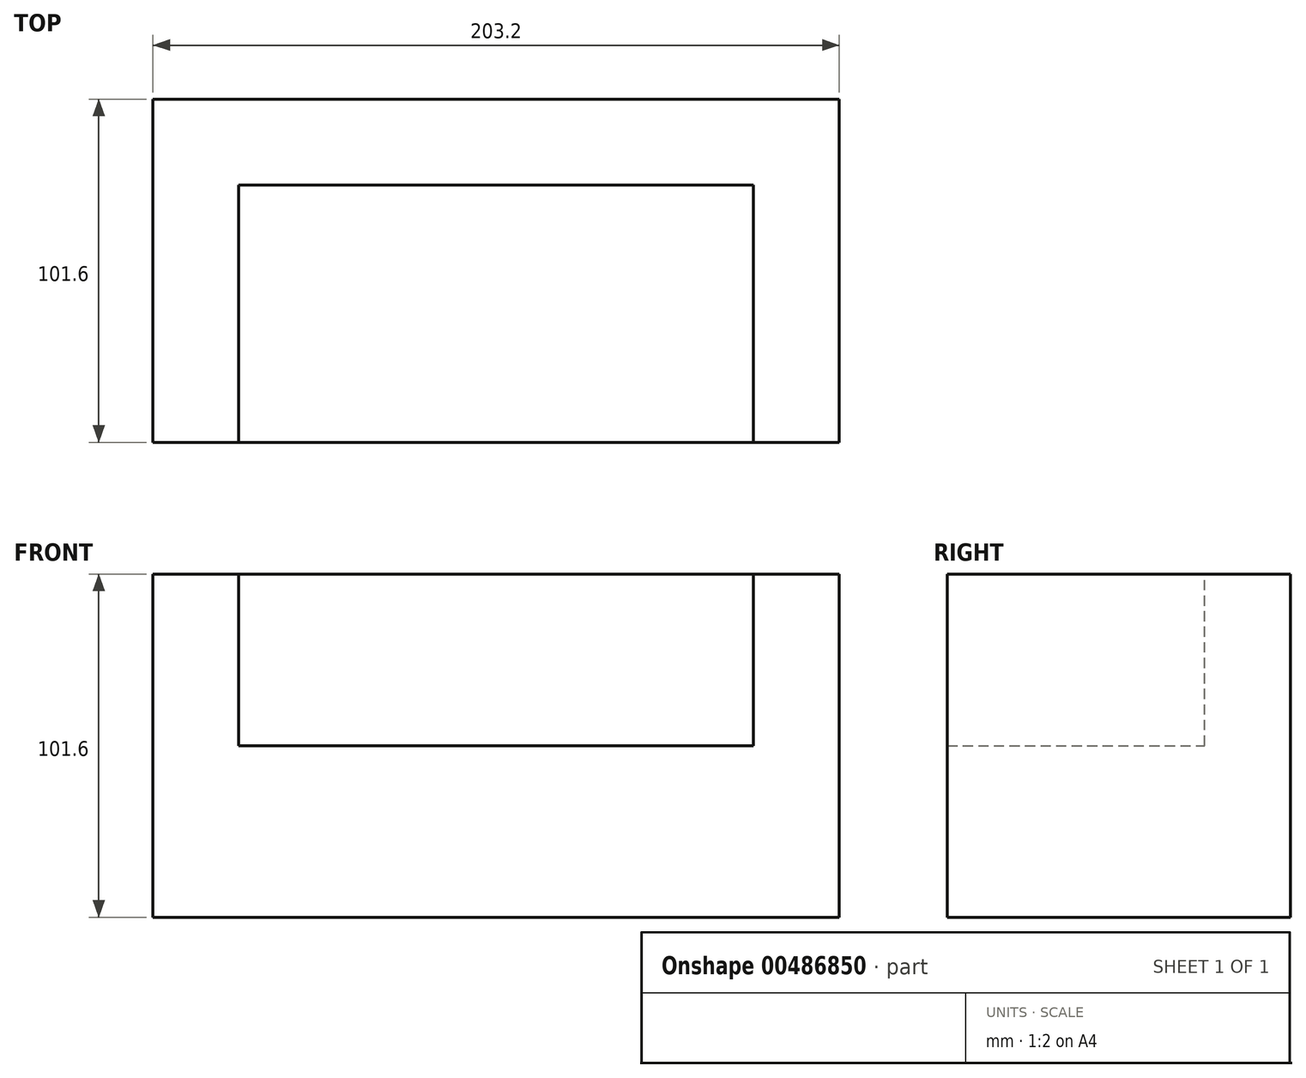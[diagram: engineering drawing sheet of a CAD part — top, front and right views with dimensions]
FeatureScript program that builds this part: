
annotation { "Feature Type Name" : "Feature", "Feature Type Description" : "" }
export const myFeature = defineFeature(function(context is Context, id is Id, definition is map)
    precondition{}
    {
        {
            var Q0;
            Q0=qCreatedBy(makeId("Top.planeOp"),FACE);
            var sketch = newSketch(context, id + "F0", { "sketchPlane" : qUnion([Q0])});
            skLineSegment(sketch, "E0.bottom", {"start": v(0, 0) * mm, "end": v(-203.2, 0) * mm});
            skLineSegment(sketch, "E0.top", {"start": v(0, 101.6) * mm, "end": v(-203.2, 101.6) * mm});
            skLineSegment(sketch, "E0.left", {"start": v(0, 0) * mm, "end": v(0, 101.6) * mm});
            skLineSegment(sketch, "E0.right", {"start": v(-203.2, 0) * mm, "end": v(-203.2, 101.6) * mm});
            skSolve(sketch);
        }
        {
            var Q0;
            Q0 = qSketchRegion(id + "F0", true);
            extrude(context, id + "F1", {"entities" : qUnion([Q0]), "depth" : 101.6 * mm});
        }
        {
            var Q0;
            Q0=makeQuery(id+"F1.opExtrude","CAP_FACE",FACE,{"disambiguationData":[OSD([sQuery(id+"F0.wireOp",EDGE,"E0.bottom"),sQuery(id+"F0.wireOp",EDGE,"E0.top"),sQuery(id+"F0.wireOp",EDGE,"E0.left"),sQuery(id+"F0.wireOp",EDGE,"E0.right")])],"isStart":false});
            var sketch = newSketch(context, id + "F2", { "sketchPlane" : qUnion([Q0])});
            skLineSegment(sketch, "E1.right", {"start": v(-25.4, 0) * mm, "end": v(-25.4, 76.2) * mm});
            skLineSegment(sketch, "E2.bottom", {"start": v(-25.4, 0) * mm, "end": v(-177.8, 0) * mm});
            skLineSegment(sketch, "E2.top", {"start": v(-25.4, 76.2) * mm, "end": v(-177.8, 76.2) * mm});
            skLineSegment(sketch, "E2.right", {"start": v(-177.8, 0) * mm, "end": v(-177.8, 76.2) * mm});
            skSolve(sketch);
        }
        {
            var Q0;
            Q0 = qSketchRegion(id + "F2", true);
            extrude(context, id + "F3", {"entities" : qUnion([Q0]), "operationType" : NewBodyOperationType.REMOVE, "oppositeDirection" : true, "depth" : 50.8 * mm});
        }
    });
